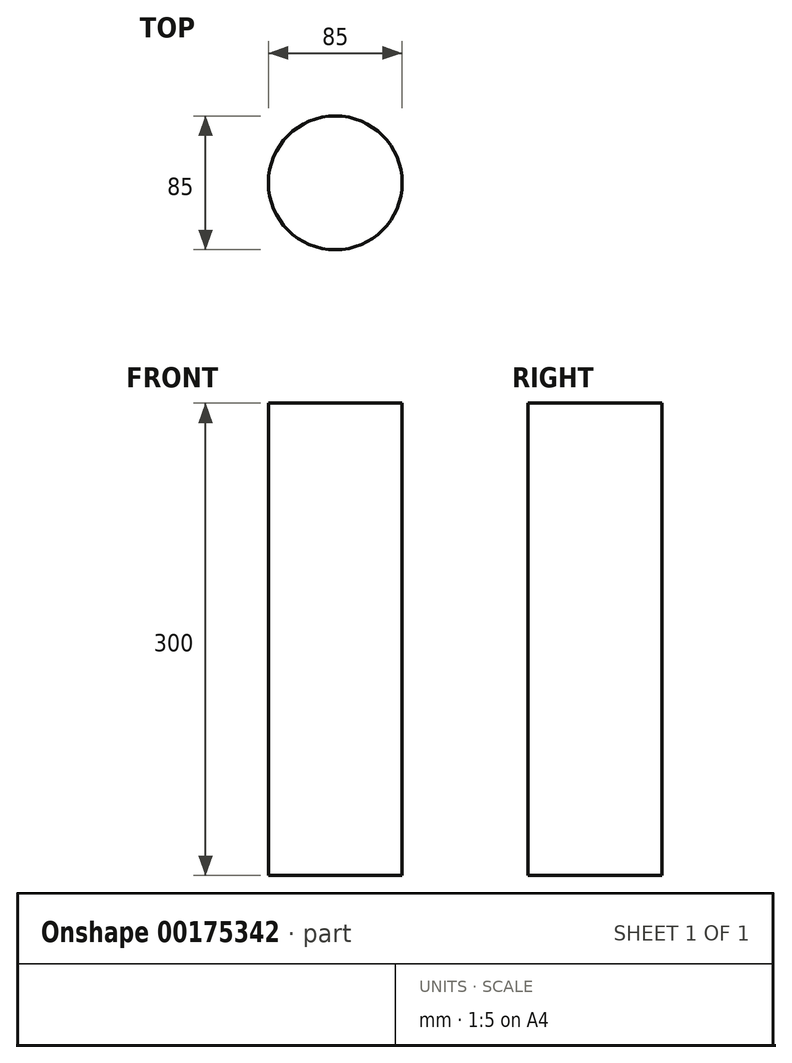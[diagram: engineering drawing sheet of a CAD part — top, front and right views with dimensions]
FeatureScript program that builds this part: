
annotation { "Feature Type Name" : "Feature", "Feature Type Description" : "" }
export const myFeature = defineFeature(function(context is Context, id is Id, definition is map)
    precondition{}
    {
        {
            var Q0;
            Q0=qCreatedBy(makeId("Top.planeOp"),FACE);
            var sketch = newSketch(context, id + "F0", { "sketchPlane" : qUnion([Q0])});
            skCircle(sketch, "E0", {"center": v(0, 0) * mm, "radius": 42.5 * mm});
            skSolve(sketch);
        }
        {
            var Q0;
            Q0 = qSketchRegion(id + "F0", true);
            extrude(context, id + "F1", {"entities" : qUnion([Q0]), "depth" : 300 * mm});
        }
    });
